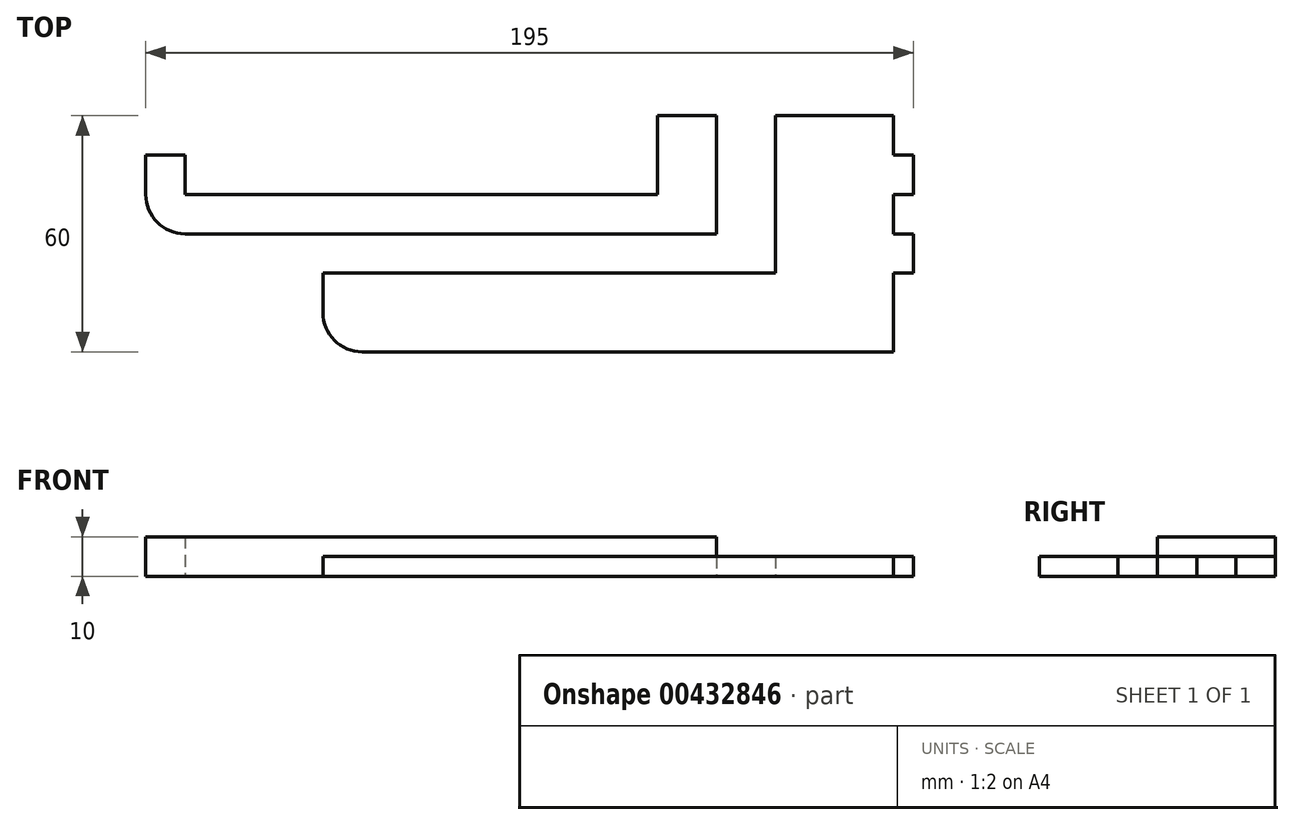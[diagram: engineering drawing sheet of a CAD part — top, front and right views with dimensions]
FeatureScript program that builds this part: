
annotation { "Feature Type Name" : "Feature", "Feature Type Description" : "" }
export const myFeature = defineFeature(function(context is Context, id is Id, definition is map)
    precondition{}
    {
        {
            var Q0;
            Q0=qCreatedBy(makeId("Top.planeOp"),FACE);
            var sketch = newSketch(context, id + "F0", { "sketchPlane" : qUnion([Q0])});
            skLineSegment(sketch, "E0.bottom", {"start": v(-60, 0) * mm, "end": v(-50, 0) * mm});
            skLineSegment(sketch, "E0.left", {"start": v(-60, 0) * mm, "end": v(-60, -10) * mm});
            skLineSegment(sketch, "E0.right", {"start": v(-50, 0) * mm, "end": v(-50, -10) * mm});
            skLineSegment(sketch, "E1.bottom", {"start": v(-50, -10) * mm, "end": v(70, -10) * mm});
            skLineSegment(sketch, "E1.top", {"start": v(-50, -20) * mm, "end": v(70, -20) * mm});
            skLineSegment(sketch, "E2.bottom", {"start": v(70, 10) * mm, "end": v(85, 10) * mm});
            skLineSegment(sketch, "E2.left", {"start": v(70, 10) * mm, "end": v(70, -10) * mm});
            skLineSegment(sketch, "E2.right", {"start": v(85, 10) * mm, "end": v(85, -10) * mm});
            skArc(sketch, "E3", {"start": v(-60, -10) * mm, "mid": v(-57.07, -17.07) * mm, "end": v(-50, -20) * mm});
            skLineSegment(sketch, "E4", {"start": v(85, -10) * mm, "end": v(85, -20) * mm});
            skLineSegment(sketch, "E5", {"start": v(85, -20) * mm, "end": v(70, -20) * mm});
            skSolve(sketch);
        }
        {
            var Q0;
            Q0=makeQuery(id+"F0.imprint","IMPRINT",FACE,{"disambiguationData":[TD([[makeQuery(id+"F0.imprint","IMPRINT",EDGE,{"derivedFrom":sQuery(id+"F0.wireOp",EDGE,"E0.bottom")}),-1.0]])]});
            extrude(context, id + "F1", {"entities" : qUnion([Q0]), "depth" : 10 * mm});
        }
        {
            var Q0;
            Q0=qCreatedBy(makeId("Top.planeOp"),FACE);
            var sketch = newSketch(context, id + "F2", { "sketchPlane" : qUnion([Q0])});
            skLineSegment(sketch, "E6.bottom", {"start": v(-15, -30) * mm, "end": v(-5, -30) * mm});
            skLineSegment(sketch, "E6.left", {"start": v(-15, -30) * mm, "end": v(-15, -40) * mm});
            skLineSegment(sketch, "E7.top", {"start": v(-5, -50) * mm, "end": v(115, -50) * mm});
            skLineSegment(sketch, "E8.bottom", {"start": v(115, 10) * mm, "end": v(130, 10) * mm});
            skLineSegment(sketch, "E8.right", {"start": v(130, 10) * mm, "end": v(130, 0) * mm});
            skArc(sketch, "E9", {"start": v(-15, -40) * mm, "mid": v(-12.07, -47.07) * mm, "end": v(-5, -50) * mm});
            skLineSegment(sketch, "E10", {"start": v(130, -30) * mm, "end": v(130, -50) * mm});
            skLineSegment(sketch, "E11", {"start": v(130, -50) * mm, "end": v(115, -50) * mm});
            skLineSegment(sketch, "E12", {"start": v(-5, -30) * mm, "end": v(100, -30) * mm});
            skLineSegment(sketch, "E13", {"start": v(130, 0) * mm, "end": v(135, 0) * mm});
            skLineSegment(sketch, "E14", {"start": v(135, 0) * mm, "end": v(135, -10) * mm});
            skLineSegment(sketch, "E15", {"start": v(135, -10) * mm, "end": v(130, -10) * mm});
            skLineSegment(sketch, "E16", {"start": v(130, -20) * mm, "end": v(135, -20) * mm});
            skLineSegment(sketch, "E17", {"start": v(135, -20) * mm, "end": v(135, -30) * mm});
            skLineSegment(sketch, "E18", {"start": v(135, -30) * mm, "end": v(130, -30) * mm});
            skLineSegment(sketch, "E19.trimOffspring", {"start": v(130, -10) * mm, "end": v(130, -20) * mm});
            skLineSegment(sketch, "E20.trimOffspring", {"start": v(130, -30) * mm, "end": v(130, -30) * mm});
            skLineSegment(sketch, "E21", {"start": v(115, 10) * mm, "end": v(100, 10) * mm});
            skLineSegment(sketch, "E22", {"start": v(100, 10) * mm, "end": v(100, -30) * mm});
            skSolve(sketch);
        }
        {
            var Q0;
            Q0=makeQuery(id+"F2.imprint","IMPRINT",FACE,{"disambiguationData":[TD([[makeQuery(id+"F2.imprint","IMPRINT",EDGE,{"derivedFrom":sQuery(id+"F2.wireOp",EDGE,"E6.bottom")}),-1.0]])]});
            extrude(context, id + "F3", {"entities" : qUnion([Q0]), "depth" : 5 * mm});
        }
    });
